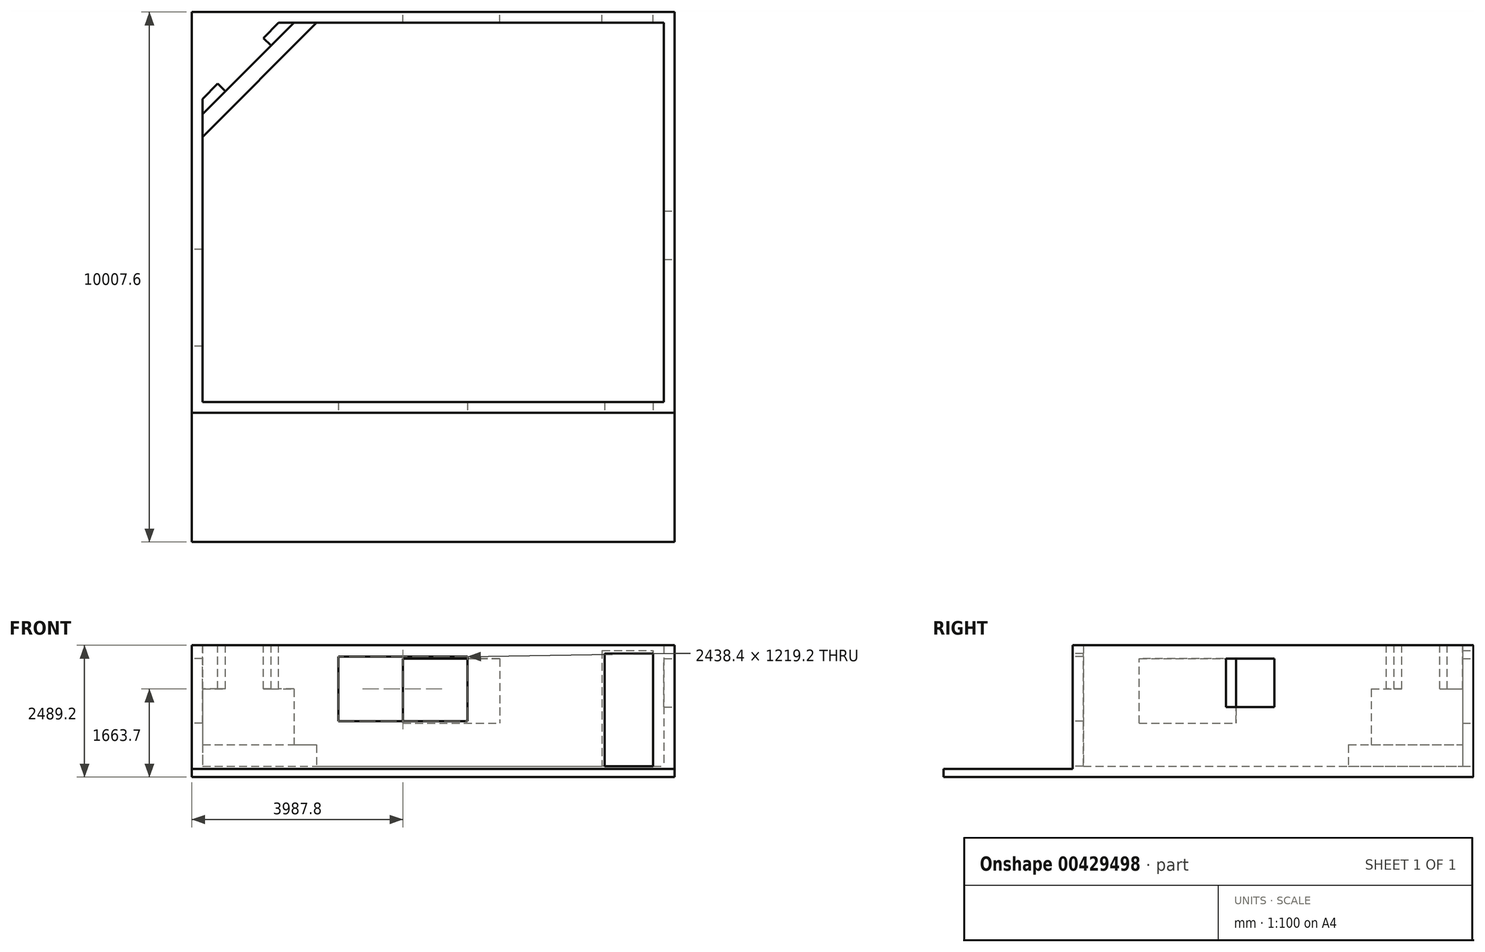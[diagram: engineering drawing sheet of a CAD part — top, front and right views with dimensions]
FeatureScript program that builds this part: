
annotation { "Feature Type Name" : "Feature", "Feature Type Description" : "" }
export const myFeature = defineFeature(function(context is Context, id is Id, definition is map)
    precondition{}
    {
        {
            var Q0;
            Q0=qCreatedBy(makeId("Top.planeOp"),FACE);
            var sketch = newSketch(context, id + "F0", { "sketchPlane" : qUnion([Q0])});
            skLineSegment(sketch, "E0.bottom", {"start": v(0, 0) * mm, "end": v(-9118.6, 0) * mm});
            skLineSegment(sketch, "E0.top", {"start": v(0, 10007.6) * mm, "end": v(-9118.6, 10007.6) * mm});
            skLineSegment(sketch, "E0.left", {"start": v(0, 0) * mm, "end": v(0, 10007.6) * mm});
            skLineSegment(sketch, "E0.right", {"start": v(-9118.6, 0) * mm, "end": v(-9118.6, 10007.6) * mm});
            skSolve(sketch);
        }
        {
            var Q0;
            Q0 = qSketchRegion(id + "F0", true);
            extrude(context, id + "F1", {"entities" : qUnion([Q0]), "oppositeDirection" : true, "depth" : 203.2 * mm});
        }
        {
            var Q0;
            Q0=makeQuery(id+"F1.opExtrude","CAP_FACE",FACE,{"disambiguationData":[OSD([sQuery(id+"F0.wireOp",EDGE,"E0.bottom"),sQuery(id+"F0.wireOp",EDGE,"E0.top"),sQuery(id+"F0.wireOp",EDGE,"E0.left"),sQuery(id+"F0.wireOp",EDGE,"E0.right")])],"isStart":true});
            var sketch = newSketch(context, id + "F2", { "sketchPlane" : qUnion([Q0])});
            skLineSegment(sketch, "E1.bottom", {"start": v(-9118.6, 0) * mm, "end": v(0, 0) * mm});
            skLineSegment(sketch, "E1.top", {"start": v(-9118.6, 2438.4) * mm, "end": v(0, 2438.4) * mm});
            skLineSegment(sketch, "E1.left", {"start": v(-9118.6, 0) * mm, "end": v(-9118.6, 2438.4) * mm});
            skLineSegment(sketch, "E1.right", {"start": v(0, 0) * mm, "end": v(0, 2438.4) * mm});
            skSolve(sketch);
        }
        {
            var Q0;
            Q0 = qSketchRegion(id + "F2", true);
            extrude(context, id + "F3", {"entities" : qUnion([Q0]), "operationType" : NewBodyOperationType.REMOVE, "oppositeDirection" : true, "depth" : 50.8 * mm});
        }
        {
            var Q0;
            Q0=makeQuery(id+"F1.opExtrude","CAP_FACE",FACE,{"disambiguationData":[OSD([sQuery(id+"F0.wireOp",EDGE,"E0.bottom"),sQuery(id+"F0.wireOp",EDGE,"E0.top"),sQuery(id+"F0.wireOp",EDGE,"E0.left"),sQuery(id+"F0.wireOp",EDGE,"E0.right")])],"isStart":true});
            var sketch = newSketch(context, id + "F4", { "sketchPlane" : qUnion([Q0])});
            skLineSegment(sketch, "E2.bottom", {"start": v(-9118.6, 2438.4) * mm, "end": v(0, 2438.4) * mm});
            skLineSegment(sketch, "E2.top", {"start": v(-9118.6, 10007.6) * mm, "end": v(0, 10007.6) * mm});
            skLineSegment(sketch, "E2.left", {"start": v(-9118.6, 2438.4) * mm, "end": v(-9118.6, 10007.6) * mm});
            skLineSegment(sketch, "E2.right", {"start": v(0, 2438.4) * mm, "end": v(0, 10007.6) * mm});
            skLineSegment(sketch, "E3.bottom", {"start": v(-8915.4, 2641.6) * mm, "end": v(-203.2, 2641.6) * mm});
            skLineSegment(sketch, "E3.top", {"start": v(-8915.4, 9804.4) * mm, "end": v(-203.2, 9804.4) * mm});
            skLineSegment(sketch, "E3.left", {"start": v(-8915.4, 2641.6) * mm, "end": v(-8915.4, 9804.4) * mm});
            skLineSegment(sketch, "E3.right", {"start": v(-203.2, 2641.6) * mm, "end": v(-203.2, 9804.4) * mm});
            skSolve(sketch);
        }
        {
            var Q0;
            Q0 = qSketchRegion(id + "F4", true);
            extrude(context, id + "F5", {"entities" : qUnion([Q0]), "operationType" : NewBodyOperationType.ADD, "depth" : 2286 * mm});
        }
        {
            var Q0;
            Q0=makeQuery(id+"F5.boolean.opBoolean","MERGE",FACE,{"derivedFrom":[makeQuery(id+"F3.boolean.opBoolean","COPY",FACE,{"derivedFrom":makeQuery(id+"F3.opExtrude","SWEPT_FACE",FACE,{"disambiguationData":[OSD([sQuery(id+"F2.wireOp",EDGE,"E1.top")])]})}),makeQuery(id+"F5.opExtrude","SWEPT_FACE",FACE,{"disambiguationData":[OSD([sQuery(id+"F4.wireOp",EDGE,"E2.bottom")])]})]});
            var sketch = newSketch(context, id + "F6", { "sketchPlane" : qUnion([Q0])});
            skLineSegment(sketch, "E4.bottom", {"start": v(-406.4, 0) * mm, "end": v(-1320.8, 0) * mm});
            skLineSegment(sketch, "E4.top", {"start": v(-406.4, 2127.25) * mm, "end": v(-1320.8, 2127.25) * mm});
            skLineSegment(sketch, "E4.left", {"start": v(-406.4, 0) * mm, "end": v(-406.4, 2127.25) * mm});
            skLineSegment(sketch, "E4.right", {"start": v(-1320.8, 0) * mm, "end": v(-1320.8, 2127.25) * mm});
            skLineSegment(sketch, "E5.bottom", {"start": v(-6350, 2070.1) * mm, "end": v(-3911.6, 2070.1) * mm});
            skLineSegment(sketch, "E5.top", {"start": v(-6350, 850.9) * mm, "end": v(-3911.6, 850.9) * mm});
            skLineSegment(sketch, "E5.left", {"start": v(-6350, 2070.1) * mm, "end": v(-6350, 850.9) * mm});
            skLineSegment(sketch, "E5.right", {"start": v(-3911.6, 2070.1) * mm, "end": v(-3911.6, 850.9) * mm});
            skSolve(sketch);
        }
        {
            var Q0;
            Q0 = qSketchRegion(id + "F6", true);
            var Q1;
            Q1=makeQuery(id+"F5.opExtrude","SWEPT_FACE",FACE,{"disambiguationData":[OSD([sQuery(id+"F4.wireOp",EDGE,"E3.bottom")])]});
            extrude(context, id + "F7", {"entities" : qUnion([Q0]), "operationType" : NewBodyOperationType.REMOVE, "endBound" : BoundingType.UP_TO_SURFACE, "oppositeDirection" : true, "endBoundEntityFace" : qUnion([Q1]), "depth" : 25.4 * mm});
        }
        {
            var Q0;
            Q0=makeQuery(id+"F5.boolean.opBoolean","MERGE",FACE,{"derivedFrom":[makeQuery(id+"F1.opExtrude","SWEPT_FACE",FACE,{"disambiguationData":[OSD([sQuery(id+"F0.wireOp",EDGE,"E0.left")])]}),makeQuery(id+"F5.opExtrude","SWEPT_FACE",FACE,{"disambiguationData":[OSD([sQuery(id+"F4.wireOp",EDGE,"E2.right")])]})]});
            var sketch = newSketch(context, id + "F8", { "sketchPlane" : qUnion([Q0])});
            skLineSegment(sketch, "E6.bottom", {"start": v(5334, 1117.6) * mm, "end": v(6248.4, 1117.6) * mm});
            skLineSegment(sketch, "E6.top", {"start": v(5334, 2032) * mm, "end": v(6248.4, 2032) * mm});
            skLineSegment(sketch, "E6.left", {"start": v(5334, 1117.6) * mm, "end": v(5334, 2032) * mm});
            skLineSegment(sketch, "E6.right", {"start": v(6248.4, 1117.6) * mm, "end": v(6248.4, 2032) * mm});
            skSolve(sketch);
        }
        {
            var Q0;
            Q0 = qSketchRegion(id + "F8", true);
            var Q1;
            Q1=makeQuery(id+"F5.opExtrude","SWEPT_FACE",FACE,{"disambiguationData":[OSD([sQuery(id+"F4.wireOp",EDGE,"E3.right")])]});
            extrude(context, id + "F9", {"entities" : qUnion([Q0]), "operationType" : NewBodyOperationType.REMOVE, "endBound" : BoundingType.UP_TO_SURFACE, "oppositeDirection" : true, "endBoundEntityFace" : qUnion([Q1]), "depth" : 25.4 * mm});
        }
        {
            var Q0;
            Q0=makeQuery(id+"F5.boolean.opBoolean","MERGE",FACE,{"derivedFrom":[makeQuery(id+"F1.opExtrude","SWEPT_FACE",FACE,{"disambiguationData":[OSD([sQuery(id+"F0.wireOp",EDGE,"E0.top")])]}),makeQuery(id+"F5.opExtrude","SWEPT_FACE",FACE,{"disambiguationData":[OSD([sQuery(id+"F4.wireOp",EDGE,"E2.top")])]})]});
            var sketch = newSketch(context, id + "F10", { "sketchPlane" : qUnion([Q0])});
            skLineSegment(sketch, "E7.bottom", {"start": v(3302, 812.8) * mm, "end": v(5130.8, 812.8) * mm});
            skLineSegment(sketch, "E7.top", {"start": v(3302, 2032) * mm, "end": v(5130.8, 2032) * mm});
            skLineSegment(sketch, "E7.left", {"start": v(3302, 812.8) * mm, "end": v(3302, 2032) * mm});
            skLineSegment(sketch, "E7.right", {"start": v(5130.8, 812.8) * mm, "end": v(5130.8, 2032) * mm});
            skSolve(sketch);
        }
        {
            var Q0;
            Q0 = qSketchRegion(id + "F10", true);
            var Q1;
            Q1=makeQuery(id+"F5.opExtrude","SWEPT_FACE",FACE,{"disambiguationData":[OSD([sQuery(id+"F4.wireOp",EDGE,"E3.top")])]});
            extrude(context, id + "F11", {"entities" : qUnion([Q0]), "operationType" : NewBodyOperationType.REMOVE, "endBound" : BoundingType.UP_TO_SURFACE, "oppositeDirection" : true, "endBoundEntityFace" : qUnion([Q1]), "depth" : 25.4 * mm});
        }
        {
            var Q0;
            Q0=makeQuery(id+"F5.boolean.opBoolean","MERGE",FACE,{"derivedFrom":[makeQuery(id+"F1.opExtrude","SWEPT_FACE",FACE,{"disambiguationData":[OSD([sQuery(id+"F0.wireOp",EDGE,"E0.top")])]}),makeQuery(id+"F5.opExtrude","SWEPT_FACE",FACE,{"disambiguationData":[OSD([sQuery(id+"F4.wireOp",EDGE,"E2.top")])]})]});
            var sketch = newSketch(context, id + "F12", { "sketchPlane" : qUnion([Q0])});
            skLineSegment(sketch, "E8.bottom", {"start": v(406.4, 0) * mm, "end": v(1371.6, 0) * mm});
            skLineSegment(sketch, "E8.top", {"start": v(406.4, 2184.4) * mm, "end": v(1371.6, 2184.4) * mm});
            skLineSegment(sketch, "E8.left", {"start": v(406.4, 0) * mm, "end": v(406.4, 2184.4) * mm});
            skLineSegment(sketch, "E8.right", {"start": v(1371.6, 0) * mm, "end": v(1371.6, 2184.4) * mm});
            skSolve(sketch);
        }
        {
            var Q0;
            Q0 = qSketchRegion(id + "F12", true);
            extrude(context, id + "F13", {"entities" : qUnion([Q0]), "operationType" : NewBodyOperationType.REMOVE, "oppositeDirection" : true, "depth" : 25.4 * mm});
        }
        {
            var Q0;
            Q0=makeQuery(id+"F5.boolean.opBoolean","MERGE",FACE,{"derivedFrom":[makeQuery(id+"F1.opExtrude","SWEPT_FACE",FACE,{"disambiguationData":[OSD([sQuery(id+"F0.wireOp",EDGE,"E0.right")])]}),makeQuery(id+"F5.opExtrude","SWEPT_FACE",FACE,{"disambiguationData":[OSD([sQuery(id+"F4.wireOp",EDGE,"E2.left")])]})]});
            var sketch = newSketch(context, id + "F14", { "sketchPlane" : qUnion([Q0])});
            skLineSegment(sketch, "E9.bottom", {"start": v(-5524.5, 2032) * mm, "end": v(-3695.7, 2032) * mm});
            skLineSegment(sketch, "E9.top", {"start": v(-5524.5, 812.8) * mm, "end": v(-3695.7, 812.8) * mm});
            skLineSegment(sketch, "E9.left", {"start": v(-5524.5, 2032) * mm, "end": v(-5524.5, 812.8) * mm});
            skLineSegment(sketch, "E9.right", {"start": v(-3695.7, 2032) * mm, "end": v(-3695.7, 812.8) * mm});
            skSolve(sketch);
        }
        {
            var Q0;
            Q0 = qSketchRegion(id + "F14", true);
            var Q1;
            Q1=makeQuery(id+"F5.opExtrude","SWEPT_FACE",FACE,{"disambiguationData":[OSD([sQuery(id+"F4.wireOp",EDGE,"E3.left")])]});
            extrude(context, id + "F15", {"entities" : qUnion([Q0]), "operationType" : NewBodyOperationType.REMOVE, "endBound" : BoundingType.UP_TO_SURFACE, "oppositeDirection" : true, "endBoundEntityFace" : qUnion([Q1]), "depth" : 25.4 * mm});
        }
        {
            var Q0;
            Q0=makeQuery(id+"F7.boolean.opBoolean","MERGE",FACE,{"derivedFrom":[makeQuery(id+"F1.opExtrude","CAP_FACE",FACE,{"disambiguationData":[OSD([sQuery(id+"F0.wireOp",EDGE,"E0.bottom"),sQuery(id+"F0.wireOp",EDGE,"E0.top"),sQuery(id+"F0.wireOp",EDGE,"E0.left"),sQuery(id+"F0.wireOp",EDGE,"E0.right")])],"isStart":true}),makeQuery(id+"F7.opExtrude","SWEPT_FACE",FACE,{"disambiguationData":[OSD([sQuery(id+"F6.wireOp",EDGE,"E4.bottom")])]})]});
            var sketch = newSketch(context, id + "F16", { "sketchPlane" : qUnion([Q0])});
            skLineSegment(sketch, "E10", {"start": v(-8915.4, 9804.4) * mm, "end": v(-8915.4, 7649.14) * mm});
            skLineSegment(sketch, "E11", {"start": v(-8915.4, 7649.14) * mm, "end": v(-6760.14, 9804.4) * mm});
            skLineSegment(sketch, "E12", {"start": v(-6760.14, 9804.4) * mm, "end": v(-8915.4, 9804.4) * mm});
            skSolve(sketch);
        }
        {
            var Q0;
            Q0 = qSketchRegion(id + "F16", true);
            extrude(context, id + "F17", {"entities" : qUnion([Q0]), "operationType" : NewBodyOperationType.ADD, "depth" : 406.4 * mm});
        }
        {
            var Q0;
            Q0=makeQuery(id+"F17.opExtrude","CAP_FACE",FACE,{"disambiguationData":[OSD([sQuery(id+"F16.wireOp",EDGE,"E10"),sQuery(id+"F16.wireOp",EDGE,"E11"),sQuery(id+"F16.wireOp",EDGE,"E12")])],"isStart":false});
            var sketch = newSketch(context, id + "F18", { "sketchPlane" : qUnion([Q0])});
            skLineSegment(sketch, "E13", {"start": v(-8915.4, 8080.2) * mm, "end": v(-7191.2, 9804.4) * mm});
            skLineSegment(sketch, "E14", {"start": v(-7191.2, 9804.4) * mm, "end": v(-8915.4, 9804.4) * mm});
            skLineSegment(sketch, "E15", {"start": v(-8915.4, 9804.4) * mm, "end": v(-8915.4, 8080.2) * mm});
            skSolve(sketch);
        }
        {
            var Q0;
            Q0 = qSketchRegion(id + "F18", true);
            var Q1;
            Q1=makeQuery(id+"F5.opExtrude","CAP_FACE",FACE,{"disambiguationData":[OSD([sQuery(id+"F4.wireOp",EDGE,"E2.bottom"),sQuery(id+"F4.wireOp",EDGE,"E2.top"),sQuery(id+"F4.wireOp",EDGE,"E2.left"),sQuery(id+"F4.wireOp",EDGE,"E2.right"),sQuery(id+"F4.wireOp",EDGE,"E3.bottom"),sQuery(id+"F4.wireOp",EDGE,"E3.top"),sQuery(id+"F4.wireOp",EDGE,"E3.left"),sQuery(id+"F4.wireOp",EDGE,"E3.right")])],"isStart":false});
            extrude(context, id + "F19", {"entities" : qUnion([Q0]), "operationType" : NewBodyOperationType.ADD, "endBound" : BoundingType.UP_TO_SURFACE, "endBoundEntityFace" : qUnion([Q1]), "depth" : 25.4 * mm});
        }
        {
            var Q0;
            {var subQ0=sQuery(id+"F4.wireOp",EDGE,"E3.right");var subQ1=sQuery(id+"F4.wireOp",EDGE,"E3.left");var subQ2=sQuery(id+"F4.wireOp",EDGE,"E3.top");var subQ3=sQuery(id+"F4.wireOp",EDGE,"E3.bottom");var subQ4=sQuery(id+"F4.wireOp",EDGE,"E2.right");var subQ5=sQuery(id+"F4.wireOp",EDGE,"E2.left");var subQ6=sQuery(id+"F4.wireOp",EDGE,"E2.top");var subQ7=sQuery(id+"F4.wireOp",EDGE,"E2.bottom");Q0=makeQuery(id+"F19.boolean.opBoolean","MERGE",FACE,{"derivedFrom":[makeQuery(id+"F5.opExtrude","CAP_FACE",FACE,{"disambiguationData":[OSD([subQ7,subQ6,subQ5,subQ4,subQ3,subQ2,subQ1,subQ0])],"isStart":false}),makeQuery(id+"F19.opExtrude","CAP_FACE",FACE,{"disambiguationData":[OSD([subQ7,subQ6,subQ5,subQ4,subQ3,subQ2,subQ1,subQ0])],"isStart":false})]});}
            var sketch = newSketch(context, id + "F20", { "sketchPlane" : qUnion([Q0])});
            skLineSegment(sketch, "E16", {"start": v(-8484.35, 8511.24) * mm, "end": v(-8915.4, 8080.2) * mm});
            skLineSegment(sketch, "E17", {"start": v(-7622.24, 9373.35) * mm, "end": v(-7191.2, 9804.4) * mm});
            skLineSegment(sketch, "E18", {"start": v(-8915.4, 8080.2) * mm, "end": v(-8915.4, 8367.56) * mm});
            skLineSegment(sketch, "E19", {"start": v(-8484.35, 8511.24) * mm, "end": v(-8628.03, 8654.93) * mm});
            skLineSegment(sketch, "E20", {"start": v(-7622.24, 9373.35) * mm, "end": v(-7765.93, 9517.03) * mm});
            skLineSegment(sketch, "E21", {"start": v(-7191.2, 9804.4) * mm, "end": v(-7478.56, 9804.4) * mm});
            skLineSegment(sketch, "E22", {"start": v(-8628.03, 8654.93) * mm, "end": v(-8915.4, 8367.56) * mm});
            skLineSegment(sketch, "E23", {"start": v(-7765.93, 9517.03) * mm, "end": v(-7478.56, 9804.4) * mm});
            skPoint(sketch, "E24.orphan", {"position": v(-7765.93, 9804.4) * mm});
            skSolve(sketch);
        }
        {
            var Q0;
            Q0 = qSketchRegion(id + "F20", true);
            extrude(context, id + "F21", {"entities" : qUnion([Q0]), "operationType" : NewBodyOperationType.REMOVE, "oppositeDirection" : true, "depth" : 825.5 * mm});
        }
        {
            var Q0;
            Q0=makeQuery(id+"F19.opExtrude","SWEPT_FACE",FACE,{"disambiguationData":[OSD([sQuery(id+"F18.wireOp",EDGE,"E13")])]});
            var sketch = newSketch(context, id + "F22", { "sketchPlane" : qUnion([Q0])});
            skLineSegment(sketch, "E25.bottom", {"start": v(222.22, 406.4) * mm, "end": v(1035.02, 406.4) * mm});
            skLineSegment(sketch, "E25.top", {"start": v(222.22, 1219.2) * mm, "end": v(1035.02, 1219.2) * mm});
            skLineSegment(sketch, "E25.left", {"start": v(222.22, 406.4) * mm, "end": v(222.22, 1219.2) * mm});
            skLineSegment(sketch, "E25.right", {"start": v(1035.02, 406.4) * mm, "end": v(1035.02, 1219.2) * mm});
            skSolve(sketch);
        }
        {
            var Q0;
            Q0=makeQuery(id+"F5.boolean.opBoolean","MERGE",FACE,{"derivedFrom":[makeQuery(id+"F1.opExtrude","SWEPT_FACE",FACE,{"disambiguationData":[OSD([sQuery(id+"F0.wireOp",EDGE,"E0.top")])]}),makeQuery(id+"F5.opExtrude","SWEPT_FACE",FACE,{"disambiguationData":[OSD([sQuery(id+"F4.wireOp",EDGE,"E2.top")])]})]});
            var sketch = newSketch(context, id + "F23", { "sketchPlane" : qUnion([Q0])});
            skLineSegment(sketch, "E26.bottom", {"start": v(406.4, 2184.4) * mm, "end": v(1371.6, 2184.4) * mm});
            skLineSegment(sketch, "E26.top", {"start": v(406.4, 0) * mm, "end": v(1371.6, 0) * mm});
            skLineSegment(sketch, "E26.left", {"start": v(406.4, 2184.4) * mm, "end": v(406.4, 0) * mm});
            skLineSegment(sketch, "E26.right", {"start": v(1371.6, 2184.4) * mm, "end": v(1371.6, 0) * mm});
            skSolve(sketch);
        }
        {
            var Q0;
            Q0 = qSketchRegion(id + "F23", true);
            var Q1;
            Q1=makeQuery(id+"F21.boolean.opBoolean","MERGE",FACE,{"derivedFrom":[makeQuery(id+"F5.opExtrude","SWEPT_FACE",FACE,{"disambiguationData":[OSD([sQuery(id+"F4.wireOp",EDGE,"E3.top")])]}),makeQuery(id+"F21.opExtrude","SWEPT_FACE",FACE,{"disambiguationData":[OSD([sQuery(id+"F20.wireOp",EDGE,"E21")])]})]});
            extrude(context, id + "F24", {"entities" : qUnion([Q0]), "operationType" : NewBodyOperationType.REMOVE, "endBound" : BoundingType.UP_TO_SURFACE, "oppositeDirection" : true, "endBoundEntityFace" : qUnion([Q1]), "depth" : 25.4 * mm});
        }
    });
